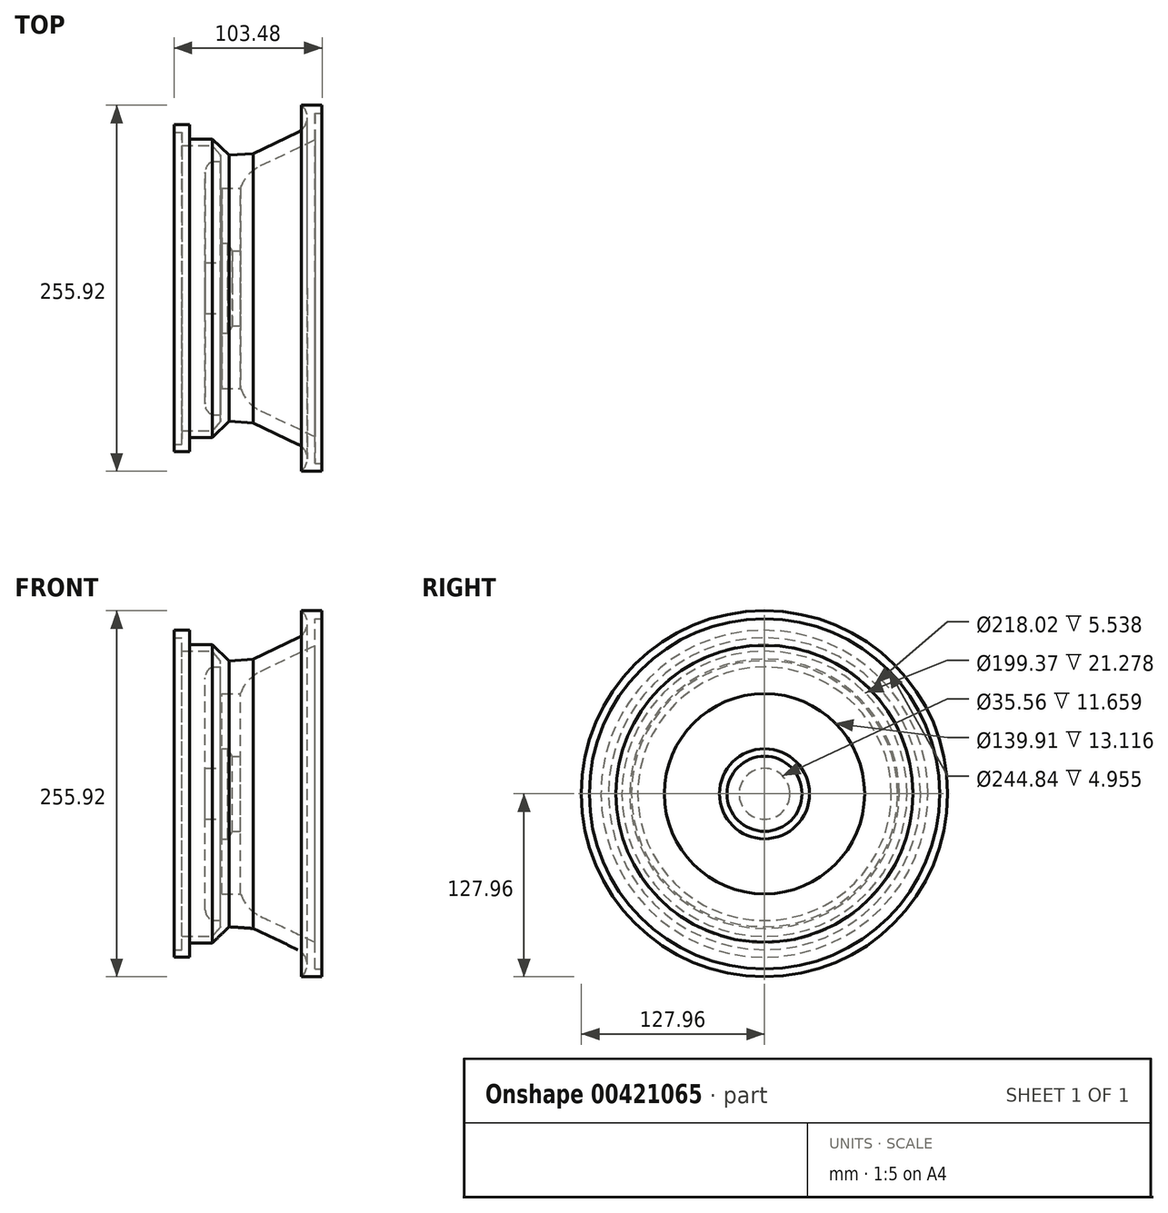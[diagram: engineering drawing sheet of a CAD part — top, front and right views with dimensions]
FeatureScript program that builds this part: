
annotation { "Feature Type Name" : "Feature", "Feature Type Description" : "" }
export const myFeature = defineFeature(function(context is Context, id is Id, definition is map)
    precondition{}
    {
        {
            var Q0;
            Q0=qCreatedBy(makeId("Front.planeOp"),FACE);
            var sketch = newSketch(context, id + "F0", { "sketchPlane" : qUnion([Q0])});
            skLineSegment(sketch, "E0", {"start": v(2.62, 33.96) * mm, "end": v(33.81, 48.82) * mm});
            skArc(sketch, "E1", {"start": v(33.81, 48.82) * mm, "mid": v(40.17, 57.66) * mm, "end": v(36.14, 67.77) * mm});
            skLineSegment(sketch, "E2", {"start": v(36.14, 67.77) * mm, "end": v(50.72, 67.77) * mm});
            skLineSegment(sketch, "E3", {"start": v(50.72, 67.77) * mm, "end": v(50.72, 62.23) * mm});
            skLineSegment(sketch, "E4", {"start": v(50.72, 62.23) * mm, "end": v(45.76, 62.23) * mm});
            skLineSegment(sketch, "E5", {"start": v(45.76, 62.23) * mm, "end": v(45.76, 43.58) * mm});
            skLineSegment(sketch, "E6", {"start": v(45.76, 43.58) * mm, "end": v(7.77, 25.47) * mm});
            skArc(sketch, "E7", {"start": v(7.77, 25.47) * mm, "mid": v(-0.77, 19.03) * mm, "end": v(-6.12, 9.76) * mm});
            skLineSegment(sketch, "E8", {"start": v(-6.12, 9.76) * mm, "end": v(-19.24, 9.76) * mm});
            skLineSegment(sketch, "E9", {"start": v(-19.24, 9.76) * mm, "end": v(-19.24, -28.71) * mm});
            skLineSegment(sketch, "E10", {"start": v(-19.24, -28.71) * mm, "end": v(-15.16, -28.71) * mm});
            skLineSegment(sketch, "E11", {"start": v(-15.16, -28.71) * mm, "end": v(-11.95, -33.96) * mm});
            skLineSegment(sketch, "E12", {"start": v(-11.95, -33.96) * mm, "end": v(-6.12, -33.96) * mm});
            skLineSegment(sketch, "E13", {"start": v(-6.12, -33.96) * mm, "end": v(-6.12, -36.29) * mm});
            skLineSegment(sketch, "E14", {"start": v(-6.12, -36.29) * mm, "end": v(-6.12, -60.19) * mm});
            skLineSegment(sketch, "E15", {"start": v(-6.12, -60.19) * mm, "end": v(-19.24, -60.19) * mm});
            skLineSegment(sketch, "E16", {"start": v(-19.24, -60.19) * mm, "end": v(-19.24, -42.4) * mm});
            skLineSegment(sketch, "E17", {"start": v(-19.24, -42.4) * mm, "end": v(-30.9, -42.4) * mm});
            skLineSegment(sketch, "E18", {"start": v(-30.9, -42.4) * mm, "end": v(-30.9, 20.84) * mm});
            skArc(sketch, "E19", {"start": v(-30.9, 20.84) * mm, "mid": v(-29.55, 25.37) * mm, "end": v(-25.94, 28.42) * mm});
            skLineSegment(sketch, "E20", {"start": v(-25.94, 28.42) * mm, "end": v(-20.11, 28.42) * mm});
            skLineSegment(sketch, "E21", {"start": v(-20.11, 28.42) * mm, "end": v(-20.11, 32.8) * mm});
            skLineSegment(sketch, "E22", {"start": v(-20.11, 32.8) * mm, "end": v(-25.94, 39.5) * mm});
            skLineSegment(sketch, "E23", {"start": v(-25.94, 39.5) * mm, "end": v(-47.22, 39.5) * mm});
            skLineSegment(sketch, "E24", {"start": v(-47.22, 39.5) * mm, "end": v(-47.22, 48.82) * mm});
            skLineSegment(sketch, "E25", {"start": v(-47.22, 48.82) * mm, "end": v(-52.76, 48.82) * mm});
            skLineSegment(sketch, "E26", {"start": v(-52.76, 48.82) * mm, "end": v(-52.76, 54.07) * mm});
            skLineSegment(sketch, "E27", {"start": v(-52.76, 54.07) * mm, "end": v(-41.68, 54.07) * mm});
            skLineSegment(sketch, "E28", {"start": v(-41.68, 54.07) * mm, "end": v(-41.68, 44.16) * mm});
            skLineSegment(sketch, "E29", {"start": v(-41.68, 44.16) * mm, "end": v(-25.94, 44.16) * mm});
            skLineSegment(sketch, "E30", {"start": v(-25.94, 44.16) * mm, "end": v(-14.28, 32.8) * mm});
            skLineSegment(sketch, "E31", {"start": v(-14.28, 32.8) * mm, "end": v(2.62, 33.96) * mm});
            skSolve(sketch);
        }
        {
            var Q0;
            Q0 = qSketchRegion(id + "F0", true);
            var Q1;
            Q1=sQuery(id+"F0.wireOp",EDGE,"E15");
            revolve(context, id + "F1", {"entities" : qUnion([Q0]), "axis" : qUnion([Q1]), "revolveType" : RevolveType.FULL});
        }
    });
